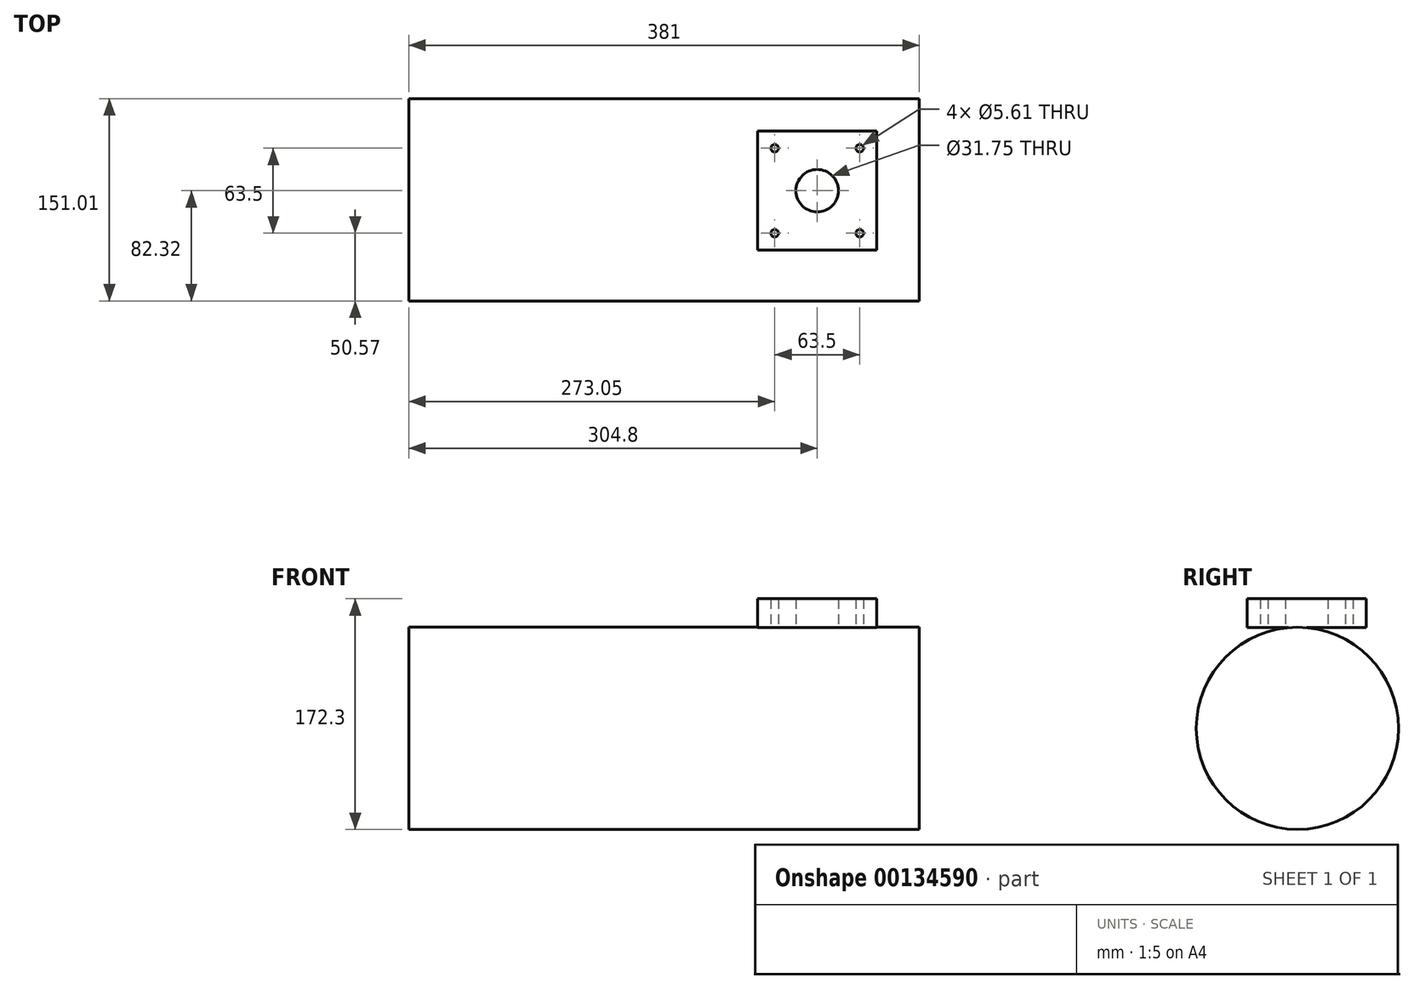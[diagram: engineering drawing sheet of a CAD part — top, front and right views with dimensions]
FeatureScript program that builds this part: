
annotation { "Feature Type Name" : "Feature", "Feature Type Description" : "" }
export const myFeature = defineFeature(function(context is Context, id is Id, definition is map)
    precondition{}
    {
        {
            var Q0;
            Q0=qCreatedBy(makeId("Top.planeOp"),FACE);
            var sketch = newSketch(context, id + "F0", { "sketchPlane" : qUnion([Q0])});
            skLineSegment(sketch, "E0.bottom", {"start": v(-44.45, 44.45) * mm, "end": v(44.45, 44.45) * mm});
            skLineSegment(sketch, "E0.top", {"start": v(-44.45, -44.45) * mm, "end": v(44.45, -44.45) * mm});
            skLineSegment(sketch, "E0.left", {"start": v(-44.45, 44.45) * mm, "end": v(-44.45, -44.45) * mm});
            skLineSegment(sketch, "E0.right", {"start": v(44.45, 44.45) * mm, "end": v(44.45, -44.45) * mm});
            skCircle(sketch, "E1", {"center": v(-31.75, 31.75) * mm, "radius": 2.8 * mm});
            skCircle(sketch, "E2", {"center": v(0, 0) * mm, "radius": 15.88 * mm});
            skCircle(sketch, "E3.0.1.0", {"center": v(-31.75, -31.75) * mm, "radius": 2.8 * mm});
            skCircle(sketch, "E3.1.0.0", {"center": v(31.75, 31.75) * mm, "radius": 2.8 * mm});
            skCircle(sketch, "E3.1.1.0", {"center": v(31.75, -31.75) * mm, "radius": 2.8 * mm});
            skLineSegment(sketch, "E3.direction1", {"start": v(-31.75, 31.75) * mm, "end": v(31.75, 31.75) * mm, "construction": true});
            skLineSegment(sketch, "E3.direction2", {"start": v(-31.75, 31.75) * mm, "end": v(-31.75, -31.75) * mm, "construction": true});
            skSolve(sketch);
        }
        {
            var Q0;
            Q0=makeQuery(id+"F0.imprint","IMPRINT",FACE,{"disambiguationData":[TD([[makeQuery(id+"F0.imprint","IMPRINT",EDGE,{"derivedFrom":sQuery(id+"F0.wireOp",EDGE,"E0.bottom")}),-1.0]])]});
            extrude(context, id + "F1", {"entities" : qUnion([Q0]), "depth" : 21.59 * mm});
        }
        {
            var Q0;
            Q0=qCreatedBy(makeId("Right.planeOp"),FACE);
            var sketch = newSketch(context, id + "F2", { "sketchPlane" : qUnion([Q0])});
            skCircle(sketch, "E4", {"center": v(-6.82, -75.2) * mm, "radius": 75.5 * mm});
            skSolve(sketch);
        }
        {
            var Q0;
            Q0=makeQuery(id+"F2.imprint","IMPRINT",FACE,{"disambiguationData":[TD([[makeQuery(id+"F2.imprint","IMPRINT",EDGE,{"derivedFrom":sQuery(id+"F2.wireOp",EDGE,"E4")}),1.0]])]});
            extrude(context, id + "F3", {"entities" : qUnion([Q0]), "depth" : 76.2 * mm, "hasSecondDirection" : true, "secondDirectionOppositeDirection" : true, "secondDirectionDepth" : 304.8 * mm});
        }
    });
